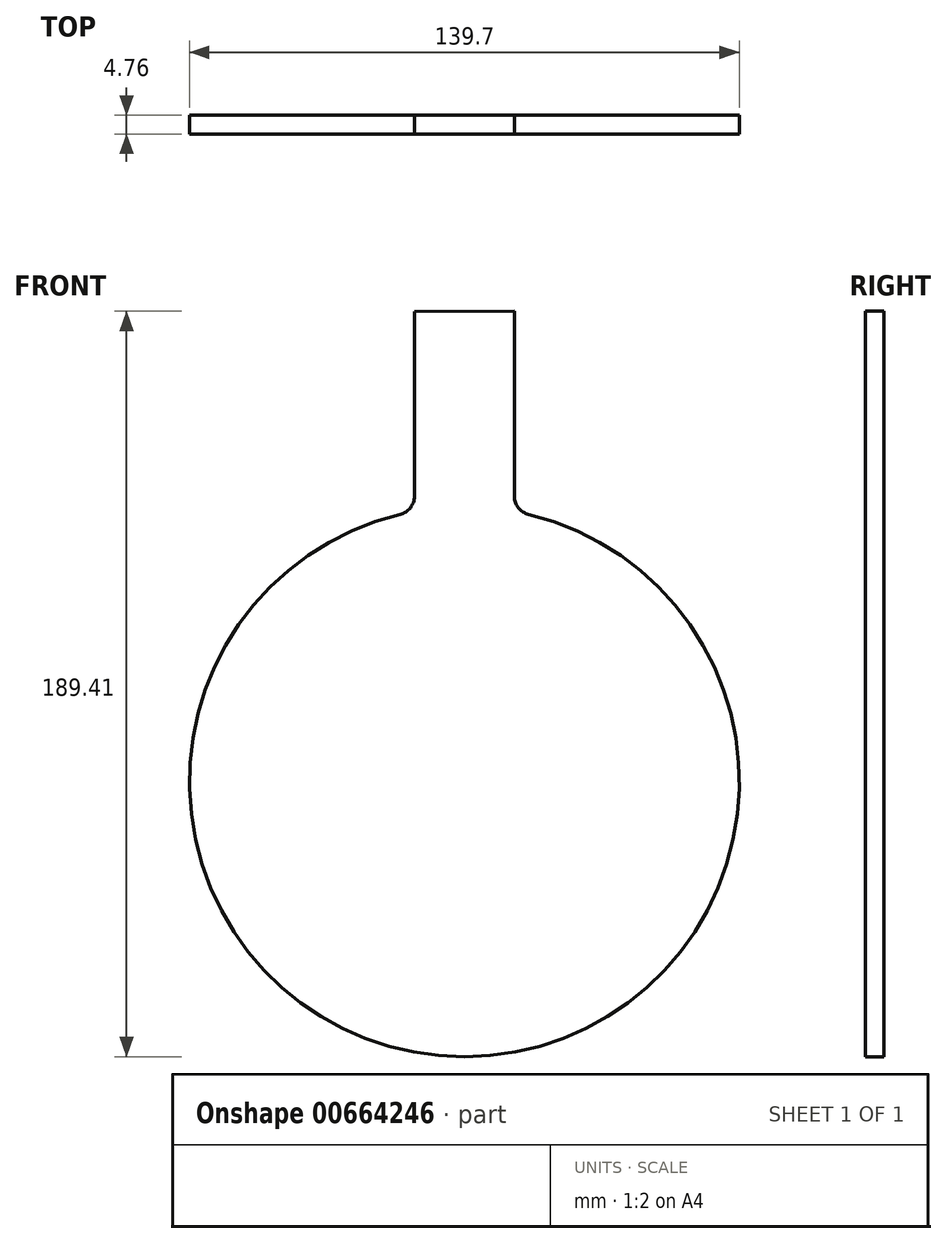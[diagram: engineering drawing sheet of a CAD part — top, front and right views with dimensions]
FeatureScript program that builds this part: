
annotation { "Feature Type Name" : "Feature", "Feature Type Description" : "" }
export const myFeature = defineFeature(function(context is Context, id is Id, definition is map)
    precondition{}
    {
        {
            var Q0;
            Q0=qCreatedBy(makeId("Front.planeOp"),FACE);
            var sketch = newSketch(context, id + "F0", { "sketchPlane" : qUnion([Q0])});
            skArc(sketch, "E0", {"start": v(-16.35, 67.91) * mm, "mid": v(0, -69.85) * mm, "end": v(16.35, 67.91) * mm});
            skLineSegment(sketch, "E1.0", {"start": v(12.7, 72.54) * mm, "end": v(12.7, 119.56) * mm});
            skLineSegment(sketch, "E2.0", {"start": v(-12.7, 72.54) * mm, "end": v(-12.7, 119.49) * mm});
            skLineSegment(sketch, "E3", {"start": v(-12.7, 119.49) * mm, "end": v(12.7, 119.56) * mm});
            skLineSegment(sketch, "E4", {"start": v(0, 119.52) * mm, "end": v(0, 0) * mm, "construction": true});
            skPoint(sketch, "E5.0.visualSharp", {"position": v(12.7, 68.69) * mm});
            skArc(sketch, "E5.0.filletArc", {"start": v(12.7, 72.54) * mm, "mid": v(13.72, 69.6) * mm, "end": v(16.35, 67.91) * mm});
            skPoint(sketch, "E6.0.visualSharp", {"position": v(-12.7, 68.69) * mm});
            skArc(sketch, "E6.0.filletArc", {"start": v(-16.35, 67.91) * mm, "mid": v(-13.72, 69.6) * mm, "end": v(-12.7, 72.54) * mm});
            skSolve(sketch);
        }
        {
            var Q0;
            Q0 = qSketchRegion(id + "F0", true);
            extrude(context, id + "F1", {"entities" : qUnion([Q0]), "flatOperationType" : FlatOperationType.REMOVE, "depth" : 4.76 * mm, "offsetDistance" : 25.4 * mm, "domain" : OperationDomain.MODEL});
        }
    });
